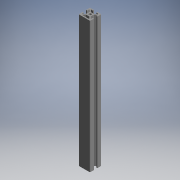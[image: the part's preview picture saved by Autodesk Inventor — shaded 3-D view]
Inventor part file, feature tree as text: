
AUTODESK INVENTOR PART (.ipt)
format: ipt  version: 2017.3 (Build 213256000, 256)  size: 202,240 bytes
history: native  units: mm (DEFAULTED — no unit token found)
features: other x7, sketch x2, extrude x1, hole x1
ambient origin geometry x8: Origin, YZ Plane, XZ Plane, XY Plane, X Axis, Y Axis, Z Axis, Center Point
bodies: Solid1 (feature_tree)
feature tree (11):
  extrude  "Extrusion1"  TaperAngle=0.0deg  [1 undecoded]
  hole  "Hole1"  [1 undecoded]
  other  "C1_XY"
  other  "C1_YZ"
  other  "C1_ZX"
  other  "C1_X"
  other  "C1_Y"
  other  "C1_Z"
  other  "C1_Center"
  sketch  "Sketch_76"  dims[d2=4.2mm d3=6.0mm d4=4.0mm d5=2.0mm d6=90.0deg d7=230.0mm d8=0.0mm d9=0.0mm]
  sketch  "Sketch2"  dims[d0=230.0mm d1=0.0mm]
note: 2 required parameter values undecoded (feature->parameter linkage not recoverable at this tier; creation-order binding heuristic only, values carry confidence <= 0.55)
